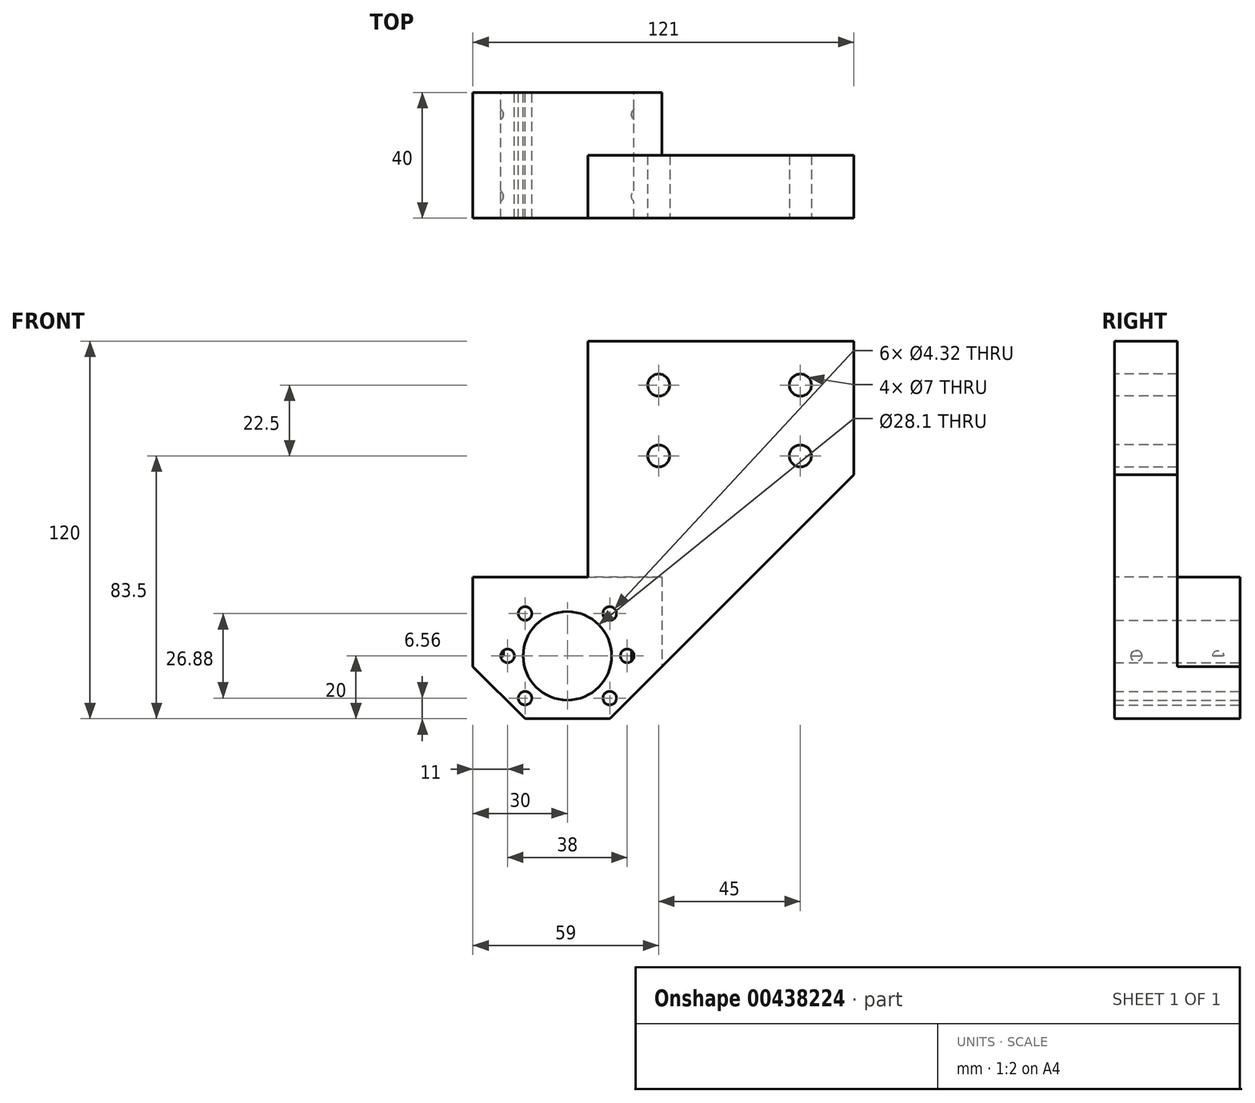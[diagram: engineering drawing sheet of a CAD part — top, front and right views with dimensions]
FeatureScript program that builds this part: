
annotation { "Feature Type Name" : "Feature", "Feature Type Description" : "" }
export const myFeature = defineFeature(function(context is Context, id is Id, definition is map)
    precondition{}
    {
        {
            var Q0;
            Q0=qCreatedBy(makeId("Front.planeOp"),FACE);
            var sketch = newSketch(context, id + "F0", { "sketchPlane" : qUnion([Q0])});
            skLineSegment(sketch, "E0.bottom", {"start": v(30, 22.5) * mm, "end": v(-30, 22.5) * mm});
            skLineSegment(sketch, "E0.top", {"start": v(30, -22.5) * mm, "end": v(-30, -22.5) * mm});
            skLineSegment(sketch, "E0.left", {"start": v(30, 22.5) * mm, "end": v(30, -22.5) * mm});
            skLineSegment(sketch, "E0.right", {"start": v(-30, 22.5) * mm, "end": v(-30, -22.5) * mm});
            skPoint(sketch, "E0.middle", {"position": v(0, 0) * mm});
            skCircle(sketch, "E1", {"center": v(0, -2.5) * mm, "radius": 14.05 * mm});
            skCircle(sketch, "E2", {"center": v(-13.44, -15.94) * mm, "radius": 2.16 * mm});
            skCircle(sketch, "E3", {"center": v(-13.44, 10.94) * mm, "radius": 2.16 * mm});
            skCircle(sketch, "E4", {"center": v(-19, -2.5) * mm, "radius": 2.16 * mm});
            skCircle(sketch, "E5", {"center": v(19, -2.5) * mm, "radius": 2.16 * mm});
            skCircle(sketch, "E6", {"center": v(13.44, 10.94) * mm, "radius": 2.16 * mm});
            skCircle(sketch, "E7", {"center": v(13.44, -15.94) * mm, "radius": 2.16 * mm});
            skLineSegment(sketch, "E8", {"start": v(30, -5.94) * mm, "end": v(13.44, -22.5) * mm, "construction": true});
            skLineSegment(sketch, "E9", {"start": v(-30, -5.94) * mm, "end": v(-13.44, -22.5) * mm, "construction": true});
            skLineSegment(sketch, "E10", {"start": v(-30, -5.94) * mm, "end": v(-13.44, -22.5) * mm});
            skLineSegment(sketch, "E11", {"start": v(30, -5.94) * mm, "end": v(13.44, -22.5) * mm});
            skSolve(sketch);
        }
        {
            var Q0;
            {var subQ0=sQuery(id+"F0.wireOp",EDGE,"E0.bottom");Q0=makeQuery(id+"F0.imprint","IMPRINT",FACE,{"disambiguationData":[TD([[makeQuery(id+"F0.imprint","IMPRINT",EDGE,{"derivedFrom":subQ0}),1.0]])]});}
            extrude(context, id + "F1", {"entities" : qUnion([Q0]), "depth" : 40 * mm});
        }
        {
            var Q0;
            Q0=makeQuery(id+"F1.opExtrude","SWEPT_FACE",FACE,{"disambiguationData":[OSD([sQuery(id+"F0.wireOp",EDGE,"E0.bottom")])]});
            var sketch = newSketch(context, id + "F2", { "sketchPlane" : qUnion([Q0])});
            skCircle(sketch, "E12", {"center": v(-22.5, -33) * mm, "radius": 2.16 * mm});
            skCircle(sketch, "E13", {"center": v(-22.5, -7) * mm, "radius": 2.16 * mm});
            skCircle(sketch, "E14", {"center": v(22.5, -7) * mm, "radius": 2.16 * mm});
            skCircle(sketch, "E15", {"center": v(22.5, -33) * mm, "radius": 2.16 * mm});
            skLineSegment(sketch, "E16", {"start": v(-30, -20) * mm, "end": v(30, -20) * mm, "construction": true});
            skLineSegment(sketch, "E17", {"start": v(0, 0) * mm, "end": v(0, -40) * mm, "construction": true});
            skSolve(sketch);
        }
        {
            var Q0;
            Q0=makeQuery(id+"F2.imprint","IMPRINT",FACE,{"disambiguationData":[TD([[makeQuery(id+"F2.imprint","IMPRINT",EDGE,{"derivedFrom":sQuery(id+"F2.wireOp",EDGE,"E13")}),1.0]])]});
            var Q1;
            Q1=makeQuery(id+"F2.imprint","IMPRINT",FACE,{"disambiguationData":[TD([[makeQuery(id+"F2.imprint","IMPRINT",EDGE,{"derivedFrom":sQuery(id+"F2.wireOp",EDGE,"E14")}),1.0]])]});
            var Q2;
            Q2=makeQuery(id+"F2.imprint","IMPRINT",FACE,{"disambiguationData":[TD([[makeQuery(id+"F2.imprint","IMPRINT",EDGE,{"derivedFrom":sQuery(id+"F2.wireOp",EDGE,"E12")}),1.0]])]});
            var Q3;
            Q3=makeQuery(id+"F2.imprint","IMPRINT",FACE,{"disambiguationData":[TD([[makeQuery(id+"F2.imprint","IMPRINT",EDGE,{"derivedFrom":sQuery(id+"F2.wireOp",EDGE,"E15")}),1.0]])]});
            extrude(context, id + "F3", {"entities" : qUnion([Q0, Q1, Q2, Q3]), "operationType" : NewBodyOperationType.REMOVE, "oppositeDirection" : true, "depth" : 15 * mm});
        }
        {
            var Q0;
            Q0=makeQuery(id+"F2.imprint","IMPRINT",FACE,{"disambiguationData":[TD([[makeQuery(id+"F2.imprint","IMPRINT",EDGE,{"derivedFrom":sQuery(id+"F2.wireOp",EDGE,"E12")}),-1.0]])]});
            var sketch = newSketch(context, id + "F4", { "sketchPlane" : qUnion([Q0])});
            skLineSegment(sketch, "E18", {"start": v(30, 0) * mm, "end": v(30, -40) * mm, "construction": true});
            skLineSegment(sketch, "E19", {"start": v(30, -20) * mm, "end": v(11, -20) * mm, "construction": true});
            skLineSegment(sketch, "E20", {"start": v(11, -20) * mm, "end": v(11, -40) * mm});
            skLineSegment(sketch, "E21", {"start": v(11, -20) * mm, "end": v(30, -20) * mm});
            skSolve(sketch);
        }
        {
            var Q0;
            Q0=makeQuery(id+"F2.imprint","IMPRINT",FACE,{"disambiguationData":[TD([[makeQuery(id+"F2.imprint","IMPRINT",EDGE,{"derivedFrom":sQuery(id+"F2.wireOp",EDGE,"E15")}),1.0]])]});
            var Q1;
            Q1=sQuery(id+"F2.wireOp",EDGE,"E15");
            extrude(context, id + "F5", {"entities" : qUnion([Q0]), "operationType" : NewBodyOperationType.ADD, "surfaceEntities" : qUnion([Q1]), "oppositeDirection" : true, "depth" : 25 * mm});
        }
        {
            var Q0;
            Q0=makeQuery(id+"F2.imprint","IMPRINT",FACE,{"disambiguationData":[TD([[makeQuery(id+"F2.imprint","IMPRINT",EDGE,{"derivedFrom":sQuery(id+"F2.wireOp",EDGE,"E12")}),-1.0]])]});
            var sketch = newSketch(context, id + "F6", { "sketchPlane" : qUnion([Q0])});
            skCircle(sketch, "E22.0", {"center": v(22.5, -7) * mm, "radius": 2.16 * mm});
            skCircle(sketch, "E23.0", {"center": v(22.5, -33) * mm, "radius": 2.16 * mm});
            skCircle(sketch, "E24.0", {"center": v(-22.5, -7) * mm, "radius": 2.16 * mm});
            skCircle(sketch, "E25.0", {"center": v(-22.5, -33) * mm, "radius": 2.16 * mm});
            skSolve(sketch);
        }
        {
            var Q0;
            Q0=qSketchRegion(id+"F6",true);
            var Q1;
            Q1=makeQuery(id+"F1.opExtrude","SWEPT_FACE",FACE,{"disambiguationData":[OSD([sQuery(id+"F0.wireOp",EDGE,"E11")])]});
            extrude(context, id + "F7", {"entities" : qUnion([Q0]), "operationType" : NewBodyOperationType.ADD, "oppositeDirection" : true, "endBoundEntityFace" : qUnion([Q1]), "depth" : 25 * mm});
        }
        {
            var Q0;
            {var subQ5=sQuery(id+"F4.wireOp",EDGE,"E20");Q0=makeQuery(id+"F4.imprint","IMPRINT",FACE,{"disambiguationData":[TD([[makeQuery(id+"F4.imprint","IMPRINT",EDGE,{"derivedFrom":subQ5}),1.0]])]});}
            extrude(context, id + "F8", {"entities" : qUnion([Q0]), "operationType" : NewBodyOperationType.ADD, "depth" : 25 * mm});
        }
        {
            var Q0;
            Q0=makeQuery(id+"F8.opExtrude","CAP_FACE",FACE,{"disambiguationData":[OSD([sQuery(id+"F0.wireOp",EDGE,"E0.bottom"),sQuery(id+"F0.wireOp",EDGE,"E0.left"),sQuery(id+"F2.wireOp",EDGE,"E15"),sQuery(id+"F4.wireOp",EDGE,"E20"),sQuery(id+"F4.wireOp",EDGE,"E21")])],"isStart":false});
            var sketch = newSketch(context, id + "F9", { "sketchPlane" : qUnion([Q0])});
            skCircle(sketch, "E26.0", {"center": v(22.5, -33) * mm, "radius": 2.16 * mm});
            skLineSegment(sketch, "E27", {"start": v(11, -20) * mm, "end": v(6.5, -20) * mm});
            skLineSegment(sketch, "E28", {"start": v(6.5, -20) * mm, "end": v(6.5, -40) * mm});
            skLineSegment(sketch, "E29", {"start": v(6.5, -40) * mm, "end": v(11, -40) * mm});
            skSolve(sketch);
        }
        {
            var Q0;
            Q0=qSketchRegion(id+"F9",true);
            extrude(context, id + "F10", {"entities" : qUnion([Q0]), "operationType" : NewBodyOperationType.ADD, "oppositeDirection" : true, "depth" : 57.1 * mm});
        }
        {
            var Q0;
            {var subQ0=sQuery(id+"F0.wireOp",EDGE,"E0.bottom");Q0=makeQuery(id+"F8.boolean.opBoolean","MERGE",FACE,{"derivedFrom":[makeQuery(id+"F1.opExtrude","CAP_FACE",FACE,{"disambiguationData":[OSD([subQ0,sQuery(id+"F0.wireOp",EDGE,"E0.top"),sQuery(id+"F0.wireOp",EDGE,"E0.left"),sQuery(id+"F0.wireOp",EDGE,"E0.right"),sQuery(id+"F0.wireOp",EDGE,"E1"),sQuery(id+"F0.wireOp",EDGE,"E2"),sQuery(id+"F0.wireOp",EDGE,"E3"),sQuery(id+"F0.wireOp",EDGE,"E4"),sQuery(id+"F0.wireOp",EDGE,"E5"),sQuery(id+"F0.wireOp",EDGE,"E6"),sQuery(id+"F0.wireOp",EDGE,"E7"),sQuery(id+"F0.wireOp",EDGE,"E10"),sQuery(id+"F0.wireOp",EDGE,"E11")])],"isStart":false}),makeQuery(id+"F8.opExtrude","SWEPT_FACE",FACE,{"disambiguationData":[OSD([subQ0])]})]});}
            var sketch = newSketch(context, id + "F11", { "sketchPlane" : qUnion([Q0])});
            skLineSegment(sketch, "E30", {"start": v(11, 47.5) * mm, "end": v(11, 97.5) * mm});
            skLineSegment(sketch, "E31", {"start": v(11, 97.5) * mm, "end": v(91, 97.5) * mm});
            skLineSegment(sketch, "E32", {"start": v(30, -5.94) * mm, "end": v(91, 55.06) * mm});
            skLineSegment(sketch, "E33", {"start": v(91, 97.5) * mm, "end": v(91, 55.06) * mm});
            skLineSegment(sketch, "E34", {"start": v(11, 97.5) * mm, "end": v(11, 83.5) * mm});
            skLineSegment(sketch, "E35", {"start": v(11, 83.5) * mm, "end": v(29, 83.5) * mm, "construction": true});
            skLineSegment(sketch, "E36", {"start": v(29, 83.5) * mm, "end": v(74, 83.5) * mm, "construction": true});
            skLineSegment(sketch, "E37", {"start": v(74, 83.5) * mm, "end": v(74, 61) * mm, "construction": true});
            skLineSegment(sketch, "E38", {"start": v(74, 61) * mm, "end": v(29, 61) * mm, "construction": true});
            skCircle(sketch, "E39", {"center": v(29, 83.5) * mm, "radius": 3.5 * mm});
            skCircle(sketch, "E40", {"center": v(74, 83.5) * mm, "radius": 3.5 * mm});
            skCircle(sketch, "E41", {"center": v(74, 61) * mm, "radius": 3.5 * mm});
            skCircle(sketch, "E42", {"center": v(29, 61) * mm, "radius": 3.5 * mm});
            skSolve(sketch);
        }
        {
            var Q0;
            Q0=makeQuery(id+"F11.imprint","IMPRINT",FACE,{"disambiguationData":[TD([[makeQuery(id+"F11.imprint","IMPRINT",EDGE,{"derivedFrom":sQuery(id+"F11.wireOp",EDGE,"E30")}),-1.0]])]});
            var Q1;
            Q1=makeQuery(id+"F8.opExtrude","CAP_VERTEX",VERTEX,{"disambiguationData":[OSD([sQuery(id+"F0.wireOp",EDGE,"E0.bottom"),sQuery(id+"F0.wireOp",EDGE,"E0.left"),sQuery(id+"F4.wireOp",EDGE,"E21")])],"isStart":false});
            extrude(context, id + "F12", {"entities" : qUnion([Q0]), "operationType" : NewBodyOperationType.ADD, "endBound" : BoundingType.UP_TO_VERTEX, "oppositeDirection" : true, "endBoundEntityVertex" : qUnion([Q1]), "depth" : 25 * mm});
        }
        {
            var Q0;
            Q0=makeQuery(id+"F9.imprint","IMPRINT",FACE,{"disambiguationData":[TD([[makeQuery(id+"F9.imprint","IMPRINT",EDGE,{"derivedFrom":sQuery(id+"F9.wireOp",EDGE,"E27")}),1.0]])]});
            extrude(context, id + "F13", {"entities" : qUnion([Q0]), "operationType" : NewBodyOperationType.ADD, "oppositeDirection" : true, "depth" : 25 * mm});
        }
        {
            var Q0;
            Q0=makeQuery(id+"F9.imprint","IMPRINT",FACE,{"disambiguationData":[TD([[makeQuery(id+"F9.imprint","IMPRINT",EDGE,{"derivedFrom":sQuery(id+"F9.wireOp",EDGE,"E27")}),1.0]])]});
            var Q1;
            Q1=makeQuery(id+"F12.opExtrude","CAP_VERTEX",VERTEX,{"disambiguationData":[OSD([sQuery(id+"F11.wireOp",EDGE,"E30"),sQuery(id+"F11.wireOp",EDGE,"E31"),sQuery(id+"F11.wireOp",EDGE,"E34"),dummyQuery(id+"F12.vertexPlane.planeOp",FACE)])],"isStart":false});
            extrude(context, id + "F14", {"entities" : qUnion([Q0]), "operationType" : NewBodyOperationType.ADD, "endBound" : BoundingType.UP_TO_VERTEX, "endBoundEntityVertex" : qUnion([Q1]), "depth" : 25 * mm});
        }
    });
